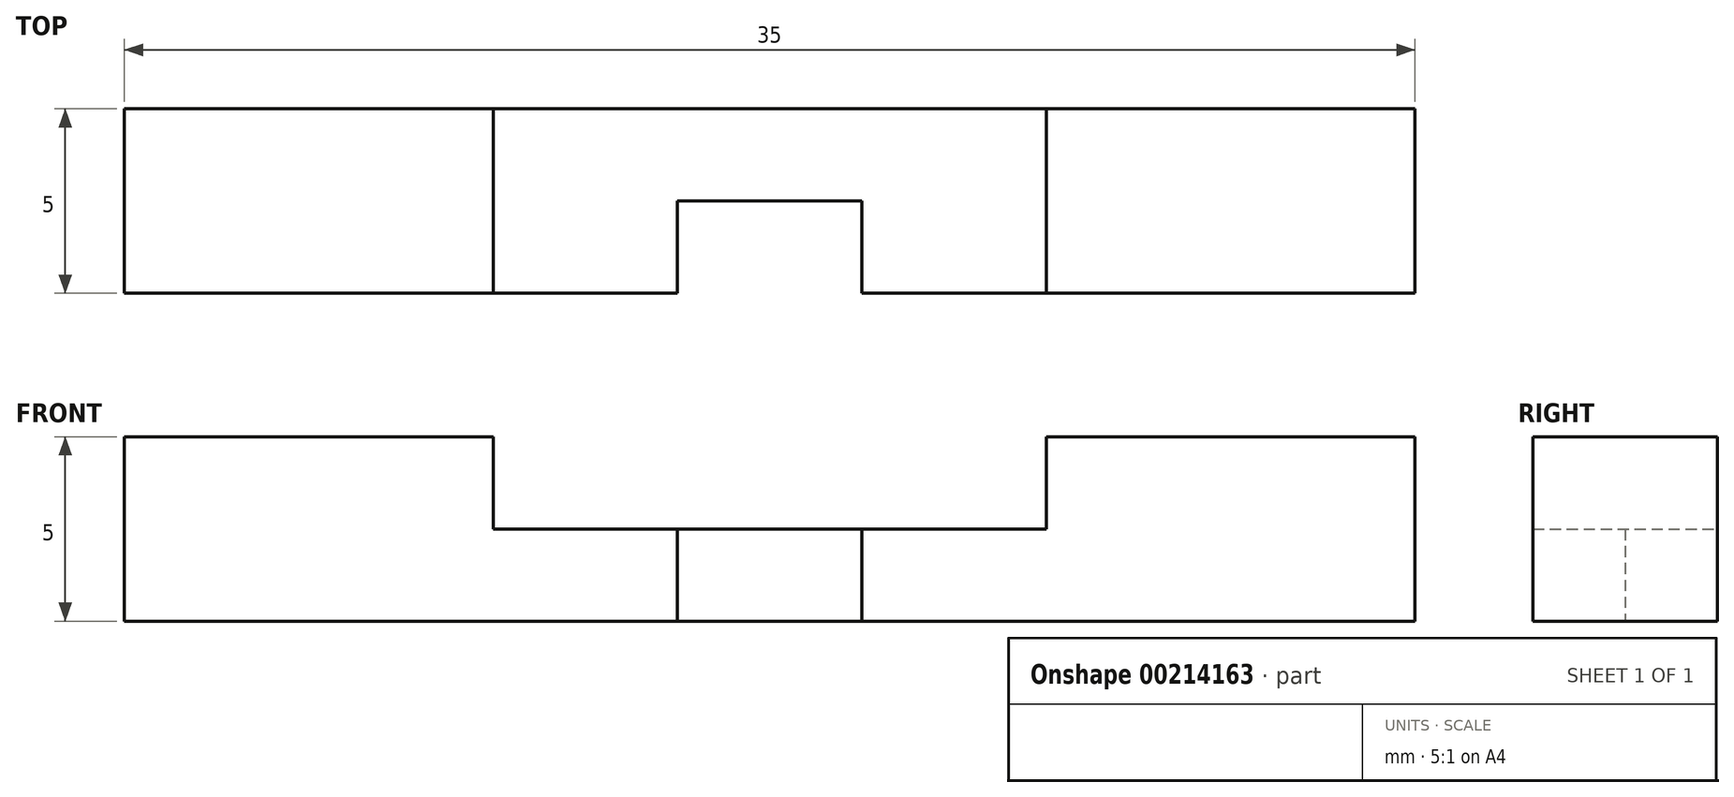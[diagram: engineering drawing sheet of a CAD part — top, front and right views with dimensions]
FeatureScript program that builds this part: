
annotation { "Feature Type Name" : "Feature", "Feature Type Description" : "" }
export const myFeature = defineFeature(function(context is Context, id is Id, definition is map)
    precondition{}
    {
        {
            var Q0;
            Q0=qCreatedBy(makeId("Top.planeOp"),FACE);
            var sketch = newSketch(context, id + "F0", { "sketchPlane" : qUnion([Q0])});
            skLineSegment(sketch, "E0.bottom", {"start": v(0, 0) * mm, "end": v(17.5, 0) * mm});
            skLineSegment(sketch, "E0.top", {"start": v(0, 5) * mm, "end": v(17.5, 5) * mm});
            skLineSegment(sketch, "E0.left", {"start": v(0, 0) * mm, "end": v(0, 5) * mm});
            skLineSegment(sketch, "E0.right", {"start": v(17.5, 0) * mm, "end": v(17.5, 5) * mm});
            skLineSegment(sketch, "E1.MirrorCS", {"start": v(0, 0) * mm, "end": v(-17.5, 0) * mm});
            skLineSegment(sketch, "E2.MirrorCS", {"start": v(0, 5) * mm, "end": v(-17.5, 5) * mm});
            skLineSegment(sketch, "E3.MirrorCS", {"start": v(-17.5, 0) * mm, "end": v(-17.5, 5) * mm});
            skSolve(sketch);
        }
        {
            var Q0;
            Q0 = qSketchRegion(id + "F0", true);
            extrude(context, id + "F1", {"entities" : qUnion([Q0]), "endBound" : BoundingType.SYMMETRIC, "depth" : 5 * mm});
        }
        {
            var Q0;
            Q0=qCreatedBy(makeId("Top.planeOp"),FACE);
            var sketch = newSketch(context, id + "F2", { "sketchPlane" : qUnion([Q0])});
            skLineSegment(sketch, "E4.bottom", {"start": v(0, 0) * mm, "end": v(7.5, 0) * mm});
            skLineSegment(sketch, "E4.top", {"start": v(0, 5) * mm, "end": v(7.5, 5) * mm});
            skLineSegment(sketch, "E4.left", {"start": v(0, 0) * mm, "end": v(0, 5) * mm});
            skLineSegment(sketch, "E4.right", {"start": v(7.5, 0) * mm, "end": v(7.5, 5) * mm});
            skLineSegment(sketch, "E5.MirrorCS", {"start": v(0, 0) * mm, "end": v(-7.5, 0) * mm});
            skLineSegment(sketch, "E6.MirrorCS", {"start": v(-7.5, 0) * mm, "end": v(-7.5, 5) * mm});
            skLineSegment(sketch, "E7.MirrorCS", {"start": v(0, 5) * mm, "end": v(-7.5, 5) * mm});
            skSolve(sketch);
        }
        {
            var Q0;
            Q0 = qSketchRegion(id + "F2", true);
            extrude(context, id + "F3", {"entities" : qUnion([Q0]), "operationType" : NewBodyOperationType.REMOVE, "depth" : 2.5 * mm});
        }
        {
            var Q0;
            Q0=qCreatedBy(makeId("Right.planeOp"),FACE);
            var sketch = newSketch(context, id + "F4", { "sketchPlane" : qUnion([Q0])});
            skLineSegment(sketch, "E8.bottom", {"start": v(0, 0) * mm, "end": v(2.5, 0) * mm});
            skLineSegment(sketch, "E8.top", {"start": v(0, -2.5) * mm, "end": v(2.5, -2.5) * mm});
            skLineSegment(sketch, "E8.left", {"start": v(0, 0) * mm, "end": v(0, -2.5) * mm});
            skLineSegment(sketch, "E8.right", {"start": v(2.5, 0) * mm, "end": v(2.5, -2.5) * mm});
            skSolve(sketch);
        }
        {
            var Q0;
            Q0 = qSketchRegion(id + "F4", true);
            extrude(context, id + "F5", {"entities" : qUnion([Q0]), "operationType" : NewBodyOperationType.REMOVE, "endBound" : BoundingType.SYMMETRIC, "oppositeDirection" : true, "depth" : 5 * mm});
        }
    });
